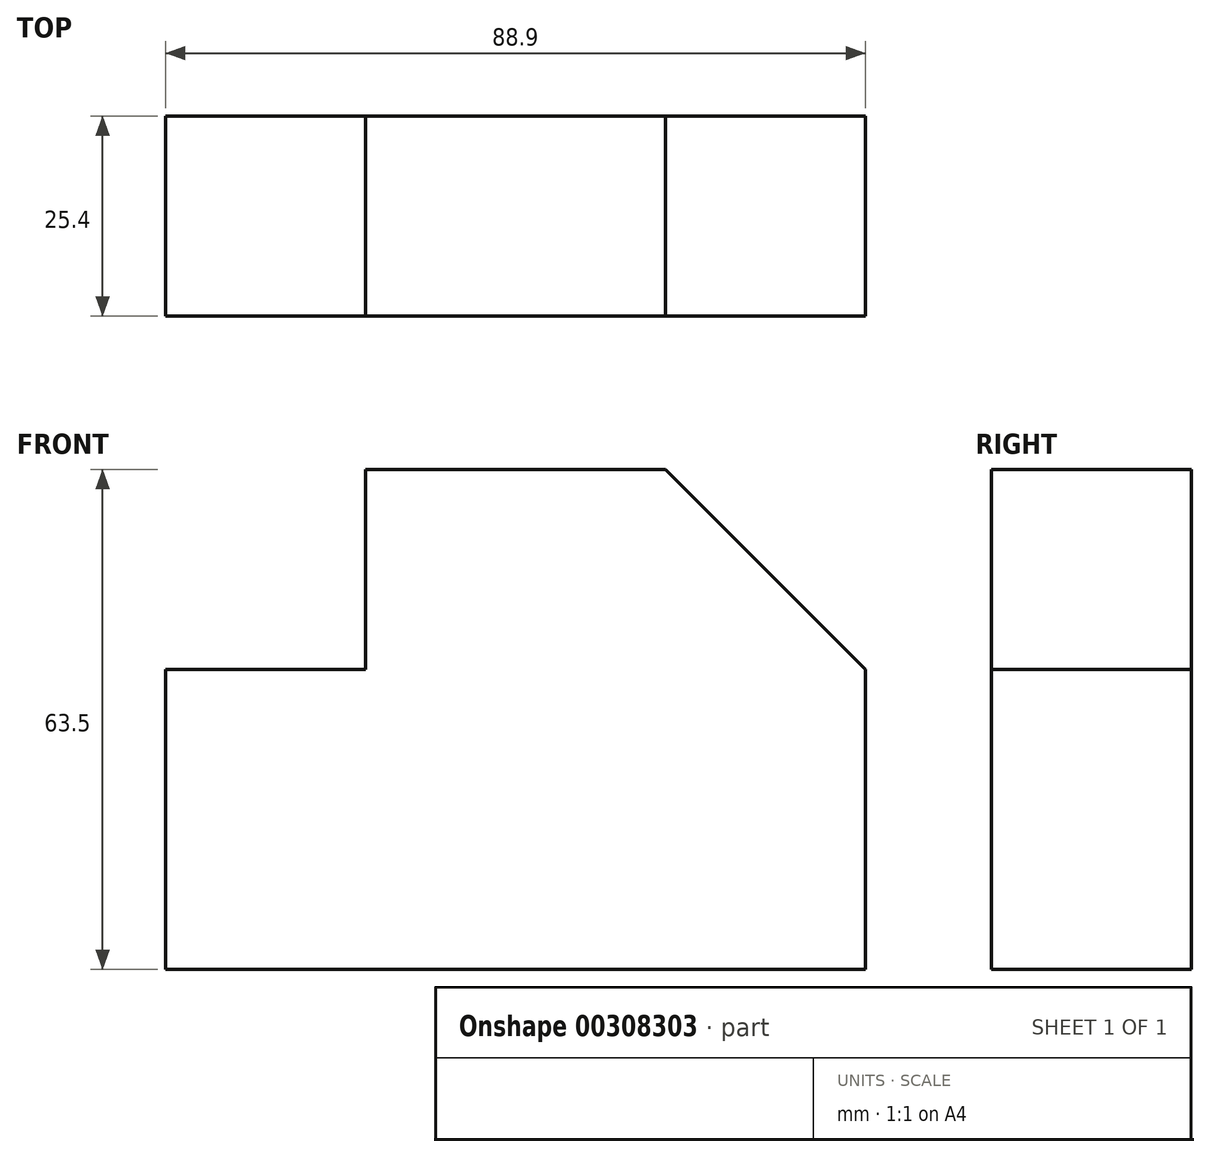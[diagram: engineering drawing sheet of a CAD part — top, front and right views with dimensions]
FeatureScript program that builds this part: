
annotation { "Feature Type Name" : "Feature", "Feature Type Description" : "" }
export const myFeature = defineFeature(function(context is Context, id is Id, definition is map)
    precondition{}
    {
        {
            var Q0;
            Q0=qCreatedBy(makeId("Front.planeOp"),FACE);
            var sketch = newSketch(context, id + "F0", { "sketchPlane" : qUnion([Q0])});
            skLineSegment(sketch, "E0", {"start": v(-47.85, -46.48) * mm, "end": v(41.05, -46.48) * mm});
            skLineSegment(sketch, "E1", {"start": v(-47.85, -46.48) * mm, "end": v(-47.85, -8.38) * mm});
            skLineSegment(sketch, "E2", {"start": v(-47.85, -8.38) * mm, "end": v(-22.45, -8.38) * mm});
            skLineSegment(sketch, "E3", {"start": v(-22.45, -8.38) * mm, "end": v(-22.45, 17.02) * mm});
            skLineSegment(sketch, "E4", {"start": v(-22.45, 17.02) * mm, "end": v(15.65, 17.02) * mm});
            skLineSegment(sketch, "E5", {"start": v(15.65, 17.02) * mm, "end": v(41.05, -8.38) * mm});
            skLineSegment(sketch, "E6", {"start": v(41.05, -8.38) * mm, "end": v(41.05, -46.48) * mm});
            skSolve(sketch);
        }
        {
            var Q0;
            Q0=makeQuery(id+"F0.imprint","IMPRINT",FACE,{"disambiguationData":[TD([[makeQuery(id+"F0.imprint","IMPRINT",EDGE,{"derivedFrom":sQuery(id+"F0.wireOp",EDGE,"E0")}),1.0]])]});
            extrude(context, id + "F1", {"entities" : qUnion([Q0]), "depth" : 25.4 * mm});
        }
    });
